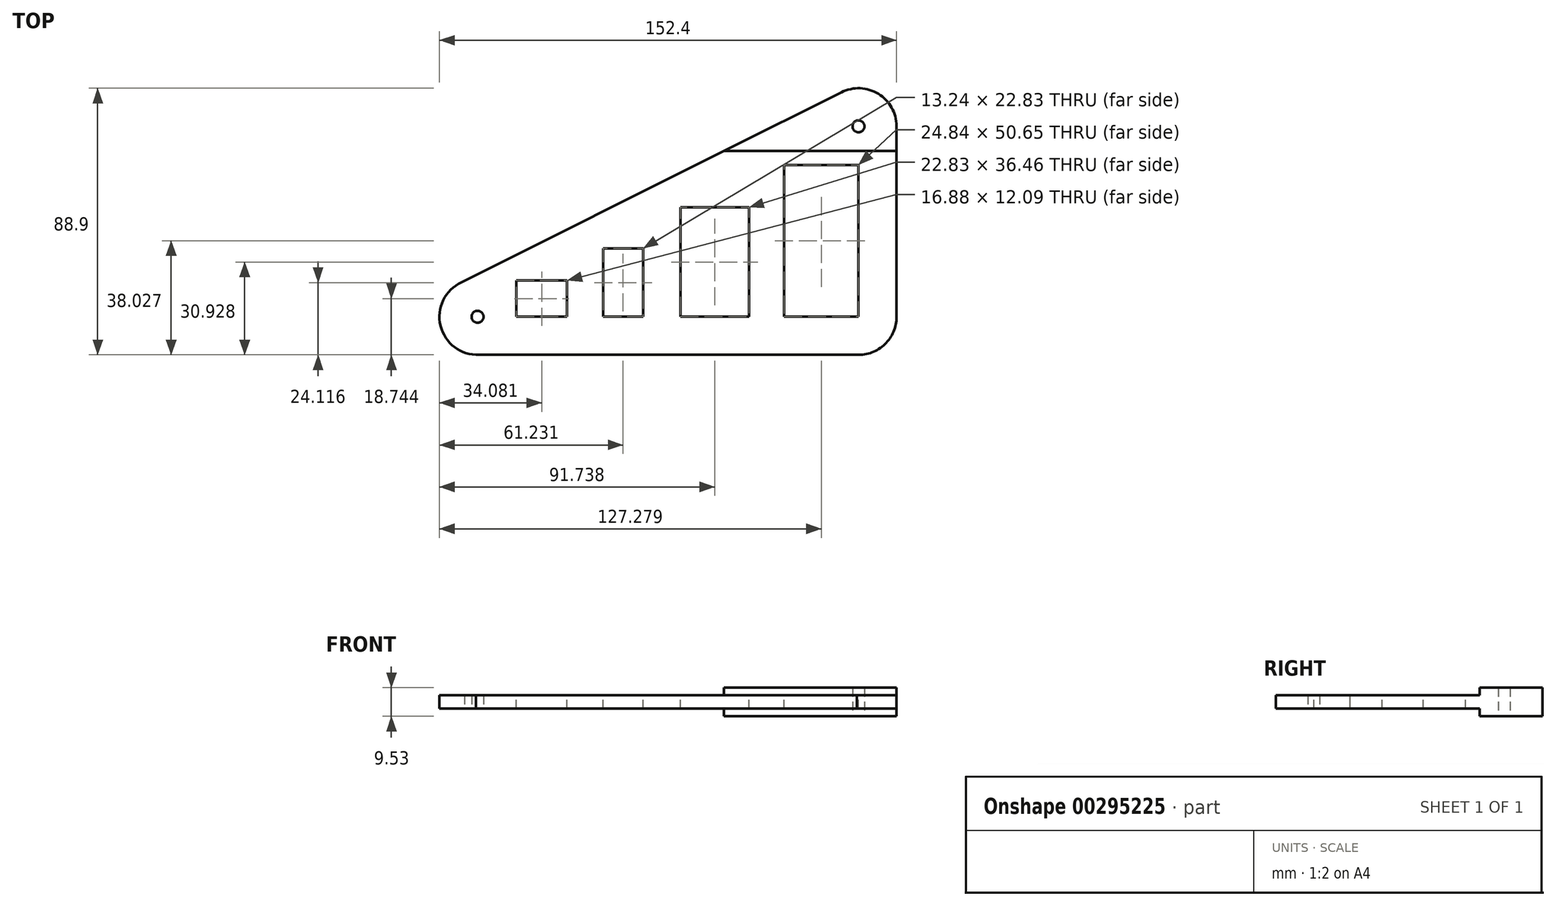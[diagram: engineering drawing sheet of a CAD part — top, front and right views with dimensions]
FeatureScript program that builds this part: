
annotation { "Feature Type Name" : "Feature", "Feature Type Description" : "" }
export const myFeature = defineFeature(function(context is Context, id is Id, definition is map)
    precondition{}
    {
        {
            var Q0;
            Q0=qCreatedBy(makeId("Top.planeOp"),FACE);
            var sketch = newSketch(context, id + "F0", { "sketchPlane" : qUnion([Q0])});
            skLineSegment(sketch, "E0", {"start": v(0, 0) * mm, "end": v(0, 63.5) * mm, "construction": true});
            skLineSegment(sketch, "E1", {"start": v(0, 0) * mm, "end": v(-127, 0) * mm, "construction": true});
            skCircle(sketch, "E2", {"center": v(-127, 0) * mm, "radius": 12.7 * mm, "construction": true});
            skCircle(sketch, "E3", {"center": v(0, 63.5) * mm, "radius": 12.7 * mm, "construction": true});
            skCircle(sketch, "E4", {"center": v(0, 0) * mm, "radius": 12.7 * mm, "construction": true});
            skLineSegment(sketch, "E5", {"start": v(12.7, 63.6) * mm, "end": v(12.7, 0) * mm});
            skLineSegment(sketch, "E6", {"start": v(-127.6, -12.69) * mm, "end": v(0, -12.69) * mm});
            skLineSegment(sketch, "E7", {"start": v(-131.36, 11.93) * mm, "end": v(-5.69, 74.86) * mm});
            skArc(sketch, "E8", {"start": v(-131.36, 11.93) * mm, "mid": v(-139.55, -1.92) * mm, "end": v(-127.6, -12.69) * mm});
            skArc(sketch, "E9", {"start": v(-5.69, 74.86) * mm, "mid": v(6.63, 74.33) * mm, "end": v(12.7, 63.6) * mm});
            skArc(sketch, "E10", {"start": v(12.7, 0) * mm, "mid": v(8.77, -9.19) * mm, "end": v(-0.6, -12.69) * mm});
            skCircle(sketch, "E11", {"center": v(-127, 0) * mm, "radius": 2 * mm});
            skCircle(sketch, "E12", {"center": v(0, 63.5) * mm, "radius": 2 * mm});
            skSolve(sketch);
        }
        {
            var Q0;
            Q0=makeQuery(id+"F0.imprint","IMPRINT",FACE,{"disambiguationData":[TD([[makeQuery(id+"F0.imprint","IMPRINT",EDGE,{"derivedFrom":sQuery(id+"F0.wireOp",EDGE,"E5")}),-1.0]])]});
            extrude(context, id + "F1", {"entities" : qUnion([Q0]), "depth" : 9.52 * mm});
        }
        {
            var Q0;
            Q0=makeQuery(id+"F1.opExtrude","SWEPT_FACE",FACE,{"disambiguationData":[OSD([sQuery(id+"F0.wireOp",EDGE,"E5")])]});
            var sketch = newSketch(context, id + "F2", { "sketchPlane" : qUnion([Q0])});
            skLineSegment(sketch, "E13.bottom", {"start": v(55.26, 0) * mm, "end": v(-16.3, 0) * mm});
            skLineSegment(sketch, "E13.top", {"start": v(55.26, 2.54) * mm, "end": v(-16.3, 2.54) * mm});
            skLineSegment(sketch, "E13.left", {"start": v(55.26, 0) * mm, "end": v(55.26, 2.54) * mm});
            skLineSegment(sketch, "E13.right", {"start": v(-16.3, 0) * mm, "end": v(-16.3, 2.54) * mm});
            skLineSegment(sketch, "E14.bottom", {"start": v(55.26, 9.53) * mm, "end": v(-16.3, 9.53) * mm});
            skLineSegment(sketch, "E14.top", {"start": v(55.26, 6.98) * mm, "end": v(-16.3, 6.98) * mm});
            skLineSegment(sketch, "E14.left", {"start": v(55.26, 9.53) * mm, "end": v(55.26, 6.98) * mm});
            skLineSegment(sketch, "E14.right", {"start": v(-16.3, 9.53) * mm, "end": v(-16.3, 6.98) * mm});
            skSolve(sketch);
        }
        {
            var Q0;
            {var subQ4=sQuery(id+"F2.wireOp",EDGE,"E14.left");Q0=makeQuery(id+"F2.imprint","IMPRINT",FACE,{"disambiguationData":[TD([[makeQuery(id+"F2.imprint","IMPRINT",EDGE,{"derivedFrom":subQ4}),-1.0]])]});}
            var Q1;
            {var subQ4=sQuery(id+"F2.wireOp",EDGE,"E13.left");Q1=makeQuery(id+"F2.imprint","IMPRINT",FACE,{"disambiguationData":[TD([[makeQuery(id+"F2.imprint","IMPRINT",EDGE,{"derivedFrom":subQ4}),1.0]])]});}
            var Q2;
            {var subQ3=sQuery(id+"F2.wireOp",EDGE,"E13.right");Q2=makeQuery(id+"F2.imprint","IMPRINT",FACE,{"disambiguationData":[TD([[makeQuery(id+"F2.imprint","IMPRINT",EDGE,{"derivedFrom":subQ3}),-1.0]])]});}
            var Q3;
            {var subQ3=sQuery(id+"F2.wireOp",EDGE,"E14.right");Q3=makeQuery(id+"F2.imprint","IMPRINT",FACE,{"disambiguationData":[TD([[makeQuery(id+"F2.imprint","IMPRINT",EDGE,{"derivedFrom":subQ3}),1.0]])]});}
            extrude(context, id + "F3", {"entities" : qUnion([Q0, Q1, Q2, Q3]), "operationType" : NewBodyOperationType.REMOVE, "endBound" : BoundingType.THROUGH_ALL, "oppositeDirection" : true, "depth" : 25.4 * mm});
        }
        {
            var Q0;
            Q0=makeQuery(id+"F3.boolean.opBoolean","COPY",FACE,{"derivedFrom":makeQuery(id+"F3.opExtrude","SWEPT_FACE",FACE,{"disambiguationData":[OSD([sQuery(id+"F2.wireOp",EDGE,"E14.top")])]})});
            var sketch = newSketch(context, id + "F4", { "sketchPlane" : qUnion([Q0])});
            skLineSegment(sketch, "E15.bottom", {"start": v(0, 0) * mm, "end": v(-24.84, 0) * mm});
            skLineSegment(sketch, "E15.top", {"start": v(0, 50.65) * mm, "end": v(-24.84, 50.65) * mm});
            skLineSegment(sketch, "E15.left", {"start": v(0, 0) * mm, "end": v(0, 50.65) * mm});
            skLineSegment(sketch, "E15.right", {"start": v(-24.84, 0) * mm, "end": v(-24.84, 50.65) * mm});
            skLineSegment(sketch, "E16.bottom", {"start": v(-36.55, 0) * mm, "end": v(-59.38, 0) * mm});
            skLineSegment(sketch, "E16.top", {"start": v(-36.55, 36.46) * mm, "end": v(-59.38, 36.46) * mm});
            skLineSegment(sketch, "E16.left", {"start": v(-36.55, 0) * mm, "end": v(-36.55, 36.46) * mm});
            skLineSegment(sketch, "E16.right", {"start": v(-59.38, 0) * mm, "end": v(-59.38, 36.46) * mm});
            skLineSegment(sketch, "E17.bottom", {"start": v(-71.85, 0) * mm, "end": v(-85.09, 0) * mm});
            skLineSegment(sketch, "E17.top", {"start": v(-71.85, 22.83) * mm, "end": v(-85.09, 22.83) * mm});
            skLineSegment(sketch, "E17.left", {"start": v(-71.85, 0) * mm, "end": v(-71.85, 22.83) * mm});
            skLineSegment(sketch, "E17.right", {"start": v(-85.09, 0) * mm, "end": v(-85.09, 22.83) * mm});
            skLineSegment(sketch, "E18.bottom", {"start": v(-97.18, 0) * mm, "end": v(-114.06, 0) * mm});
            skLineSegment(sketch, "E18.top", {"start": v(-97.18, 12.09) * mm, "end": v(-114.06, 12.09) * mm});
            skLineSegment(sketch, "E18.left", {"start": v(-97.18, 0) * mm, "end": v(-97.18, 12.09) * mm});
            skLineSegment(sketch, "E18.right", {"start": v(-114.06, 0) * mm, "end": v(-114.06, 12.09) * mm});
            skSolve(sketch);
        }
        {
            var Q0;
            Q0=makeQuery(id+"F4.imprint","IMPRINT",FACE,{"disambiguationData":[TD([[makeQuery(id+"F4.imprint","IMPRINT",EDGE,{"derivedFrom":sQuery(id+"F4.wireOp",EDGE,"E18.bottom")}),-1.0]])]});
            var Q1;
            Q1=makeQuery(id+"F4.imprint","IMPRINT",FACE,{"disambiguationData":[TD([[makeQuery(id+"F4.imprint","IMPRINT",EDGE,{"derivedFrom":sQuery(id+"F4.wireOp",EDGE,"E17.bottom")}),-1.0]])]});
            var Q2;
            Q2=makeQuery(id+"F4.imprint","IMPRINT",FACE,{"disambiguationData":[TD([[makeQuery(id+"F4.imprint","IMPRINT",EDGE,{"derivedFrom":sQuery(id+"F4.wireOp",EDGE,"E16.bottom")}),-1.0]])]});
            var Q3;
            Q3=makeQuery(id+"F4.imprint","IMPRINT",FACE,{"disambiguationData":[TD([[makeQuery(id+"F4.imprint","IMPRINT",EDGE,{"derivedFrom":sQuery(id+"F4.wireOp",EDGE,"E15.bottom")}),-1.0]])]});
            extrude(context, id + "F5", {"entities" : qUnion([Q0, Q1, Q2, Q3]), "operationType" : NewBodyOperationType.REMOVE, "oppositeDirection" : true, "depth" : 25.4 * mm});
        }
    });
